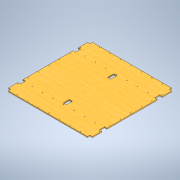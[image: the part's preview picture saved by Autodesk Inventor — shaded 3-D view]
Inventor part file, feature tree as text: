
AUTODESK INVENTOR PART (.ipt)
format: ipt  version: 2021.3 (Build 253353000, 353)  size: 245,760 bytes
history: native  units: mm
features: sketch x1, extrude x1
ambient origin geometry x8: Origin, YZ Plane, XZ Plane, XY Plane, X Axis, Y Axis, Z Axis, Center Point
bodies: Solid1 (feature_tree)
feature tree (2):
  sketch  "Sketch1"  dims[d0=700.0mm d1=700.0mm d2=21.0mm d3=21.0mm d4=40.0mm d6=360.0deg d8=21.0mm d9=99.0mm d10=141.0mm d11=8.0mm d12=0.0mm d13=10.0mm d14=4.0mm d15=4.0mm d16=4.0mm d17=175.0mm d18=87.5mm d19=87.5mm d20=4.0mm d21=40.0mm d23=360.0deg d25=130.0mm d26=120.0mm d27=60.0mm d28=140.0mm d29=25.0mm d30=50.0mm]
  extrude  "Extrusion1"  Depth=700.0mm
